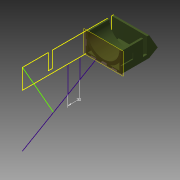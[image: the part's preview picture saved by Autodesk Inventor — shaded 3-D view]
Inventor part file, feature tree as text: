
AUTODESK INVENTOR PART (.ipt)
format: ipt  version: 2013 (Build 170138000, 138)  size: 318,464 bytes
history: native  units: mm
features: sketch x17, extrude x16, other x2
ambient origin geometry x8: Origin, YZ Plane, XZ Plane, XY Plane, X Axis, Y Axis, Z Axis, Center Point
feature tree (35):
  other  "ソリッド1"
  extrude  "押し出し1"  Depth=90.0mm
  extrude  "押し出し2"  Depth=50.0mm
  extrude  "押し出し3"  Depth=5.0mm
  extrude  "押し出し4"  Depth=85.0mm
  extrude  "押し出し6"  Depth=5.0mm
  sketch  "スケッチ9"
  extrude  "押し出し8"  Depth=80.0mm
  extrude  "押し出し9"  Depth=10.0mm
  extrude  "押し出し10"  Depth=90.0mm
  extrude  "押し出し11"  Depth=230.0mm TaperAngle=0.0deg
  extrude  "押し出し12"  Depth=225.0mm TaperAngle=0.0deg
  extrude  "押し出し13"  Depth=5.0mm TaperAngle=0.0deg
  extrude  "押し出し14"  Depth=65.0mm
  extrude  "押し出し15"  Depth=10.0mm
  other  "作業平面2"
  extrude  "押し出し16"  Depth=140.0mm
  extrude  "押し出し17"  Depth=10.0mm
  extrude  "押し出し18"  Depth=40.0mm
  sketch  "スケッチ1"
  sketch  "スケッチ2"
  sketch  "スケッチ3"
  sketch  "スケッチ4"
  sketch  "スケッチ6"
  sketch  "スケッチ12"
  sketch  "スケッチ13"
  sketch  "スケッチ14"
  sketch  "スケッチ16"
  sketch  "スケッチ17"
  sketch  "スケッチ18"
  sketch  "スケッチ19"
  sketch  "スケッチ20"
  sketch  "スケッチ21"
  sketch  "スケッチ22"
  sketch  "スケッチ23"
